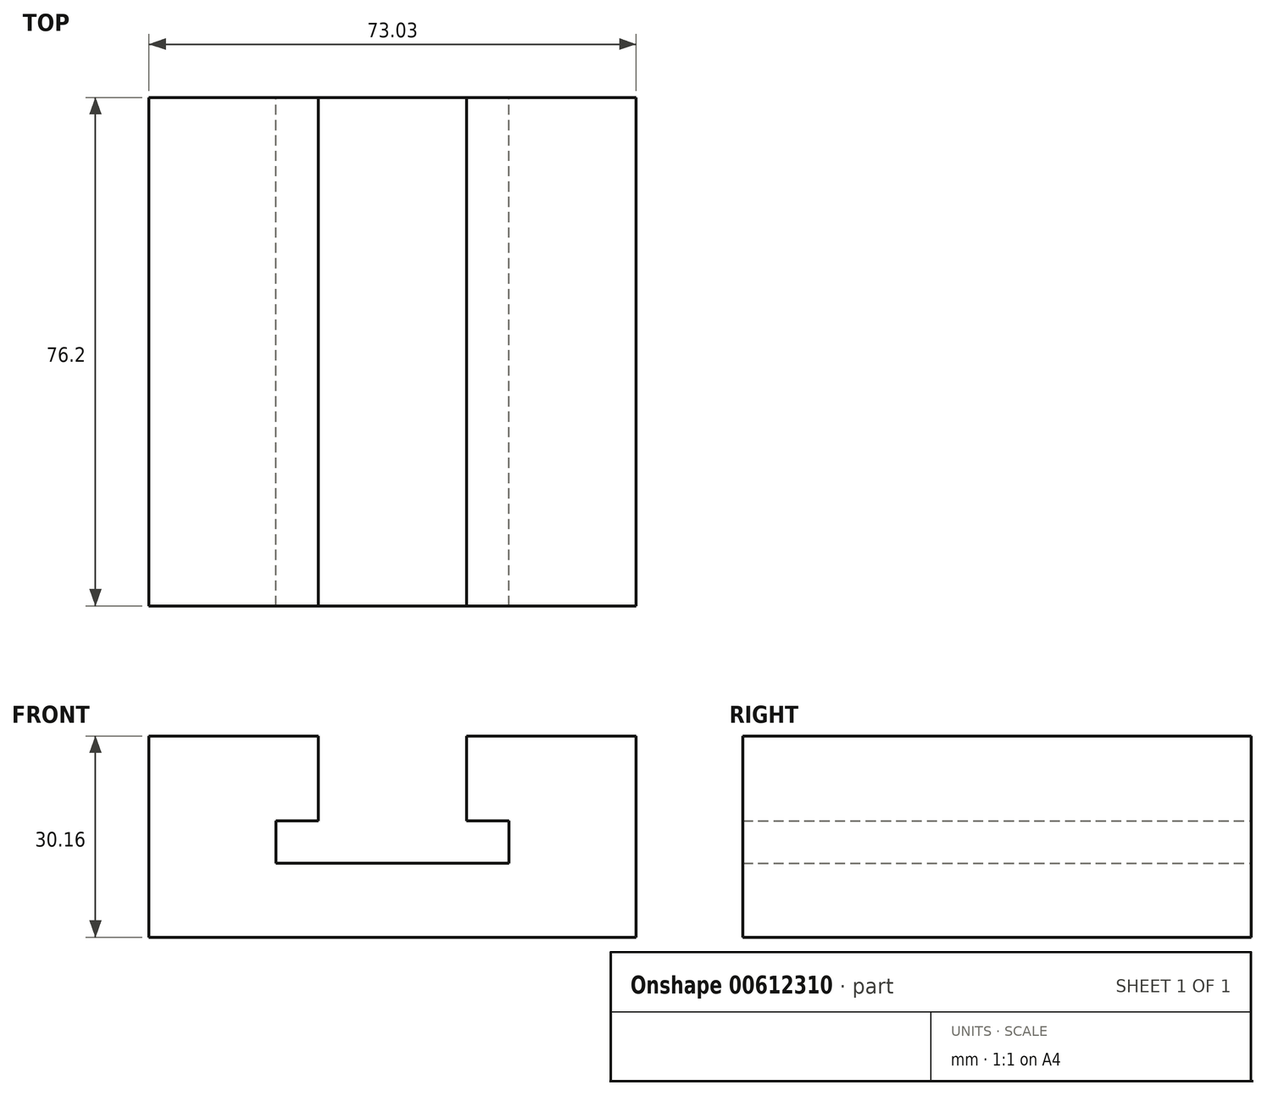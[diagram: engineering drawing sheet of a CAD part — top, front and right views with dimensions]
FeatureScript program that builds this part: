
annotation { "Feature Type Name" : "Feature", "Feature Type Description" : "" }
export const myFeature = defineFeature(function(context is Context, id is Id, definition is map)
    precondition{}
    {
        {
            var Q0;
            Q0=qCreatedBy(makeId("Front.planeOp"),FACE);
            var sketch = newSketch(context, id + "F0", { "sketchPlane" : qUnion([Q0])});
            skLineSegment(sketch, "E0", {"start": v(0, 0) * mm, "end": v(0, 30.16) * mm});
            skLineSegment(sketch, "E1", {"start": v(0, 30.16) * mm, "end": v(25.4, 30.16) * mm});
            skLineSegment(sketch, "E2", {"start": v(25.4, 30.16) * mm, "end": v(25.4, 17.46) * mm});
            skLineSegment(sketch, "E3", {"start": v(25.4, 17.46) * mm, "end": v(19.05, 17.46) * mm});
            skLineSegment(sketch, "E4", {"start": v(19.05, 17.46) * mm, "end": v(19.05, 11.11) * mm});
            skLineSegment(sketch, "E5", {"start": v(19.05, 11.11) * mm, "end": v(53.98, 11.11) * mm});
            skLineSegment(sketch, "E6", {"start": v(53.98, 11.11) * mm, "end": v(53.98, 17.46) * mm});
            skLineSegment(sketch, "E7", {"start": v(53.98, 17.46) * mm, "end": v(47.62, 17.46) * mm});
            skLineSegment(sketch, "E8", {"start": v(47.62, 17.46) * mm, "end": v(47.62, 30.16) * mm});
            skLineSegment(sketch, "E9", {"start": v(47.62, 30.16) * mm, "end": v(73.03, 30.16) * mm});
            skLineSegment(sketch, "E10", {"start": v(73.03, 30.16) * mm, "end": v(73.03, 0) * mm});
            skLineSegment(sketch, "E11", {"start": v(73.03, 0) * mm, "end": v(0, 0) * mm});
            skSolve(sketch);
        }
        {
            var Q0;
            Q0=makeQuery(id+"F0.imprint","IMPRINT",FACE,{"disambiguationData":[TD([[makeQuery(id+"F0.imprint","IMPRINT",EDGE,{"derivedFrom":sQuery(id+"F0.wireOp",EDGE,"E0")}),-1.0]])]});
            extrude(context, id + "F1", {"entities" : qUnion([Q0]), "depth" : 76.2 * mm, "offsetDistance" : 25.4 * mm});
        }
    });
